# Revit family: Heating_CFWH_Rheem_Electric
name_source: partatom
category: Mechanical Equipment
units: mm (PartAtom-declared; Revit-internal decimal feet)

## family parameters
Classification = None
Cut with Voids When Loaded = No
Host = Face
OmniClass Number = 23.65.35.11.14
OmniClass Title = Instantaneous Water Heaters
Part Type = Normal
Room Calculation Point = No
Round Connector Dimension = Use Diameter
Shared = No

## types (6) — shared parameters
Default Elevation = 1200 mm
Depth_ANZRS = 95 mm
Description = Rheem Continuous Flow Electric Water Heater
ElementMaterial = Ni80Cr20
Frequency_ANZRS = 50 Hz
Height_ANZRS = 470 mm  [stored 1.54199 ft]
Manufacturer = Rheem
Material_ANZRS = Plastic_Rheem_White_Glossy
Model = Continuous Flow Electric Water Heater
ModifiedIssue_ANZRS = 20210524 $
NumberOfPoles_ANZRS = 3
PipeNominalDiameter = 15 mm
PowerFactor_ANZRS = 1
TemperatureControl = Thermostatic
Type Comments = Suitable for indoor installations only
URL = https://www.rheem.com.au
Voltage_ANZRS = 415 V
WaterResistivity = ≥800Ω.cm
Width_ANZRS = 226 mm  [stored 0.74147 ft]

## per-type parameters (varying)
| type | 18kW | 27kW | ApparentCurrent_ANZRS | NumberOfElements | ProductCode_ANZRS | Wattage_ANZRS |
| 18kW_45°C | Yes | No | 26 A | 3 | 6C318450A | 18 kW |
| 18kW_50°C | Yes | No | 26 A | 3 | 6C318500A 
6C318600A | 18 kW |
| 18kW_60°C | Yes | No | 26 A | 3 | 6C318600A | 18 kW |
| 27kW_45°C | No | Yes | 38 A | 4 | 6C327450A | 27 kW |
| 27kW_50°C | No | Yes | 38 A | 4 | 6C327500A | 27 kW |
| 27kW_60°C | No | Yes | 38 A | 4 | 6C327600A | 27 kW |

note: [stored X ft] marks values corroborated as IEEE doubles in the binary element streams (Revit-internal decimal feet)

## geometry (parser evidence)
native form markers: Sweep x7
no freeform markers — native parametric forms only
